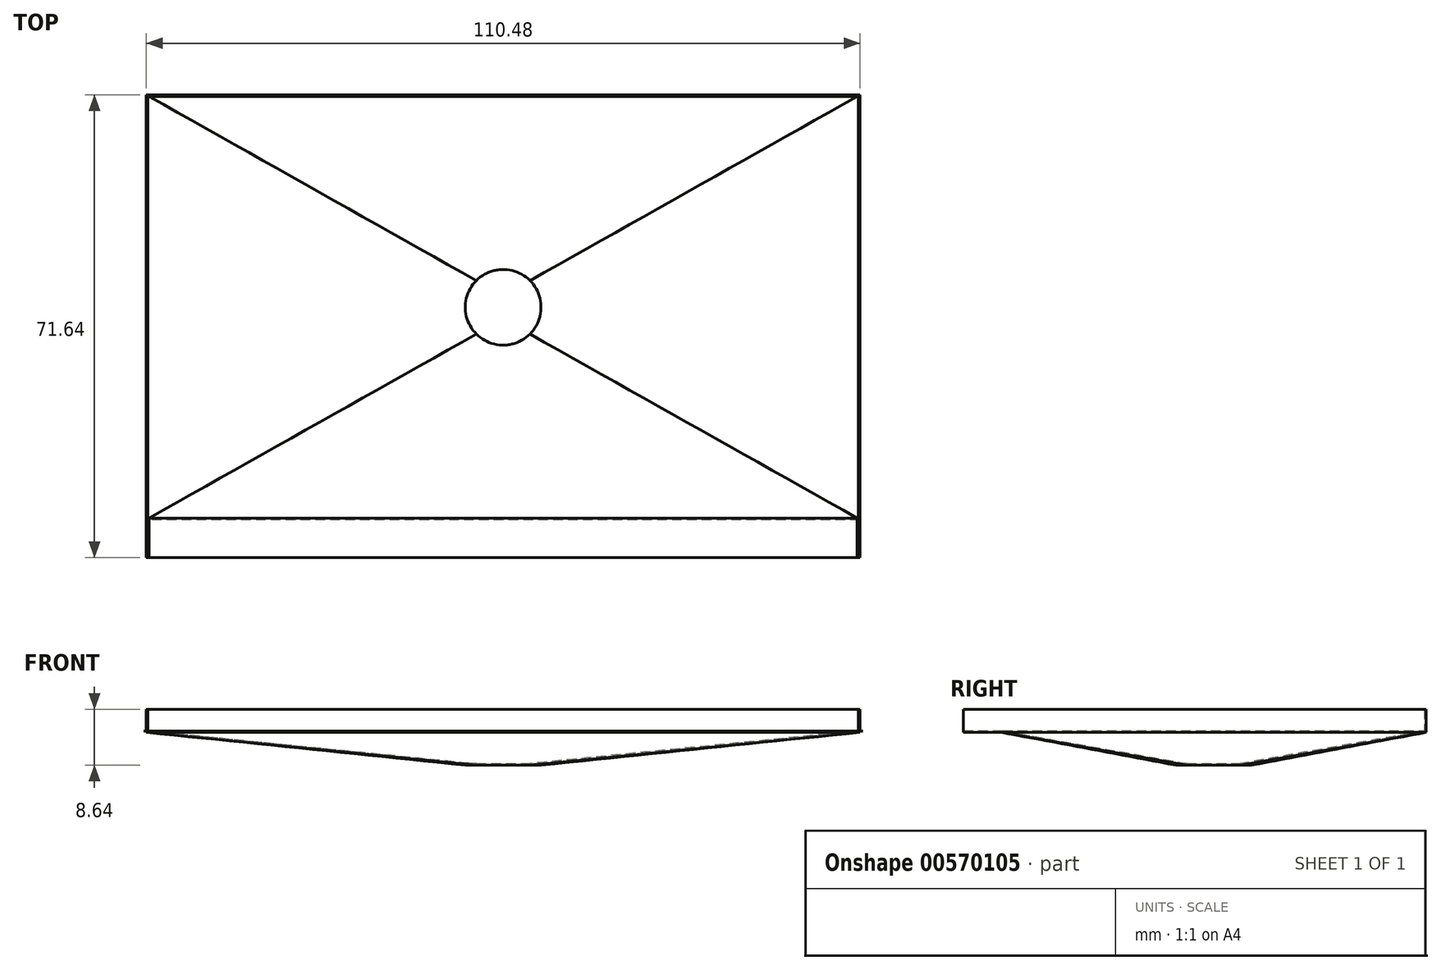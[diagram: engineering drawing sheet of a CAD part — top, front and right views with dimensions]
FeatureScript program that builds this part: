
annotation { "Feature Type Name" : "Feature", "Feature Type Description" : "" }
export const myFeature = defineFeature(function(context is Context, id is Id, definition is map)
    precondition{}
    {
        {
            var Q0;
            Q0=qCreatedBy(makeId("Top.planeOp"),FACE);
            cPlane(context, id + "F0", {"entities" : qUnion([Q0]), "cplaneType" : CPlaneType.OFFSET, "offset" : 5.08 * mm, "oppositeDirection" : true, "width" : 152.4 * mm, "height" : 152.4 * mm});
        }
        {
            var Q0;
            Q0=qCreatedBy(makeId("Top.planeOp"),FACE);
            var sketch = newSketch(context, id + "F1", { "sketchPlane" : qUnion([Q0])});
            skLineSegment(sketch, "E0.bottom", {"start": v(55.24, 32.9) * mm, "end": v(-55.24, 32.9) * mm});
            skLineSegment(sketch, "E0.top", {"start": v(55.24, -32.9) * mm, "end": v(-55.24, -32.9) * mm});
            skLineSegment(sketch, "E0.left", {"start": v(55.24, 32.9) * mm, "end": v(55.24, -32.9) * mm});
            skLineSegment(sketch, "E0.right", {"start": v(-55.24, 32.9) * mm, "end": v(-55.24, -32.9) * mm});
            skPoint(sketch, "E0.middle", {"position": v(0, 0) * mm});
            skSolve(sketch);
        }
        {
            var Q0;
            Q0=qCreatedBy(id+"F0.planeOp",FACE);
            var sketch = newSketch(context, id + "F2", { "sketchPlane" : qUnion([Q0])});
            skPoint(sketch, "E1.0", {"position": v(0, 0) * mm});
            skCircle(sketch, "E2", {"center": v(0, 0) * mm, "radius": 5.88 * mm});
            skLineSegment(sketch, "E3.bottom", {"start": v(4.16, 4.16) * mm, "end": v(-4.16, 4.16) * mm, "construction": true});
            skLineSegment(sketch, "E3.top", {"start": v(4.16, -4.16) * mm, "end": v(-4.16, -4.16) * mm, "construction": true});
            skLineSegment(sketch, "E3.left", {"start": v(4.16, 4.16) * mm, "end": v(4.16, -4.16) * mm, "construction": true});
            skLineSegment(sketch, "E3.right", {"start": v(-4.16, 4.16) * mm, "end": v(-4.16, -4.16) * mm, "construction": true});
            skSolve(sketch);
        }
        {
            var Q0;
            Q0=makeQuery(id+"F1.imprint","IMPRINT",FACE,{"disambiguationData":[TD([[makeQuery(id+"F1.imprint","IMPRINT",EDGE,{"derivedFrom":sQuery(id+"F1.wireOp",EDGE,"E0.bottom")}),1.0]])]});
            var Q1;
            Q1=makeQuery(id+"F2.imprint","IMPRINT",FACE,{"disambiguationData":[TD([[makeQuery(id+"F2.imprint","IMPRINT",EDGE,{"derivedFrom":sQuery(id+"F2.wireOp",EDGE,"E2")}),1.0]])]});
            var Q2;
            Q2=makeQuery(id+"F1.imprint","IMPRINT",FACE,{"disambiguationData":[TD([[makeQuery(id+"F1.imprint","IMPRINT",EDGE,{"derivedFrom":sQuery(id+"F1.wireOp",EDGE,"E0.bottom")}),1.0]])]});
            var Q3;
            Q3=makeQuery(id+"F2.imprint","IMPRINT",FACE,{"disambiguationData":[TD([[makeQuery(id+"F2.imprint","IMPRINT",EDGE,{"derivedFrom":sQuery(id+"F2.wireOp",EDGE,"E2")}),1.0]])]});
            var Q4;
            Q4=sQuery(id+"F2.wireOp",VERTEX,"E3.left.start");
            var Q5;
            Q5=sQuery(id+"F1.wireOp",VERTEX,"E0.left.start");
            loft(context, id + "F3", {"sheetProfilesArray" : [{ "sheetProfileEntities" : qUnion([Q0]) }, { "sheetProfileEntities" : qUnion([Q1]) }], "wireProfilesArray" : [{ "wireProfileEntities" : qUnion([Q2]) }, { "wireProfileEntities" : qUnion([Q3]) }], "matchConnections" : true, "connections" : [{ "connectionEntities" : qUnion([Q4, Q5]), "connectionEdgeQueries" : qUnion([]), "connectionEdgeParameters" : [] }]});
        }
        {
            var Q0;
            Q0=makeQuery(id+"F3.opLoft","CAP_FACE",FACE,{"disambiguationData":[OSD([makeQuery(id+"F1.imprint","IMPRINT",FACE,{"disambiguationData":[TD([[makeQuery(id+"F1.imprint","IMPRINT",EDGE,{"derivedFrom":sQuery(id+"F1.wireOp",EDGE,"E0.bottom")}),1.0]])]})])],"isStart":true});
            extrude(context, id + "F4", {"entities" : qUnion([Q0]), "operationType" : NewBodyOperationType.ADD, "depth" : 3.56 * mm, "offsetDistance" : 25.4 * mm});
        }
        {
            var Q0;
            Q0=makeQuery(id+"F4.opExtrude","CAP_FACE",FACE,{"disambiguationData":[OSD([makeQuery(id+"F1.imprint","IMPRINT",FACE,{"disambiguationData":[TD([[makeQuery(id+"F1.imprint","IMPRINT",EDGE,{"derivedFrom":sQuery(id+"F1.wireOp",EDGE,"E0.bottom")}),1.0]])]})])],"isStart":false});
            shell(context, id + "F5", {"entities" : qUnion([Q0]), "thickness" : 0.25 * mm});
        }
        {
            var Q0;
            Q0=makeQuery(id+"F5.opShell","OFFSET_FACE",FACE,{"disambiguationData":[OSD([makeQuery(id+"F2.imprint","IMPRINT",FACE,{"disambiguationData":[TD([[makeQuery(id+"F2.imprint","IMPRINT",EDGE,{"derivedFrom":sQuery(id+"F2.wireOp",EDGE,"E2")}),1.0]])]})])]});
            extrude(context, id + "F6", {"entities" : qUnion([Q0]), "operationType" : NewBodyOperationType.REMOVE, "endBound" : BoundingType.UP_TO_NEXT, "oppositeDirection" : true, "depth" : 25.4 * mm, "offsetDistance" : 25.4 * mm});
        }
        {
            var Q0;
            Q0=makeQuery(id+"F5.opShell","OFFSET_FACE",FACE,{"disambiguationData":[OSD([sQuery(id+"F1.wireOp",EDGE,"E0.top"),sQuery(id+"F1.wireOp",EDGE,"E0.left"),sQuery(id+"F1.wireOp",EDGE,"E0.right")])]});
            extrude(context, id + "F7", {"entities" : qUnion([Q0]), "operationType" : NewBodyOperationType.REMOVE, "endBound" : BoundingType.UP_TO_NEXT, "oppositeDirection" : true, "depth" : 25.4 * mm, "offsetDistance" : 25.4 * mm});
        }
        {
            var Q0;
            Q0=makeQuery(id+"F4.opExtrude","SWEPT_FACE",FACE,{"disambiguationData":[OSD([sQuery(id+"F1.wireOp",EDGE,"E0.top"),sQuery(id+"F1.wireOp",EDGE,"E0.left"),sQuery(id+"F1.wireOp",EDGE,"E0.right")])]});
            extrude(context, id + "F8", {"entities" : qUnion([Q0]), "operationType" : NewBodyOperationType.ADD, "depth" : 5.84 * mm, "offsetDistance" : 25.4 * mm});
        }
    });
